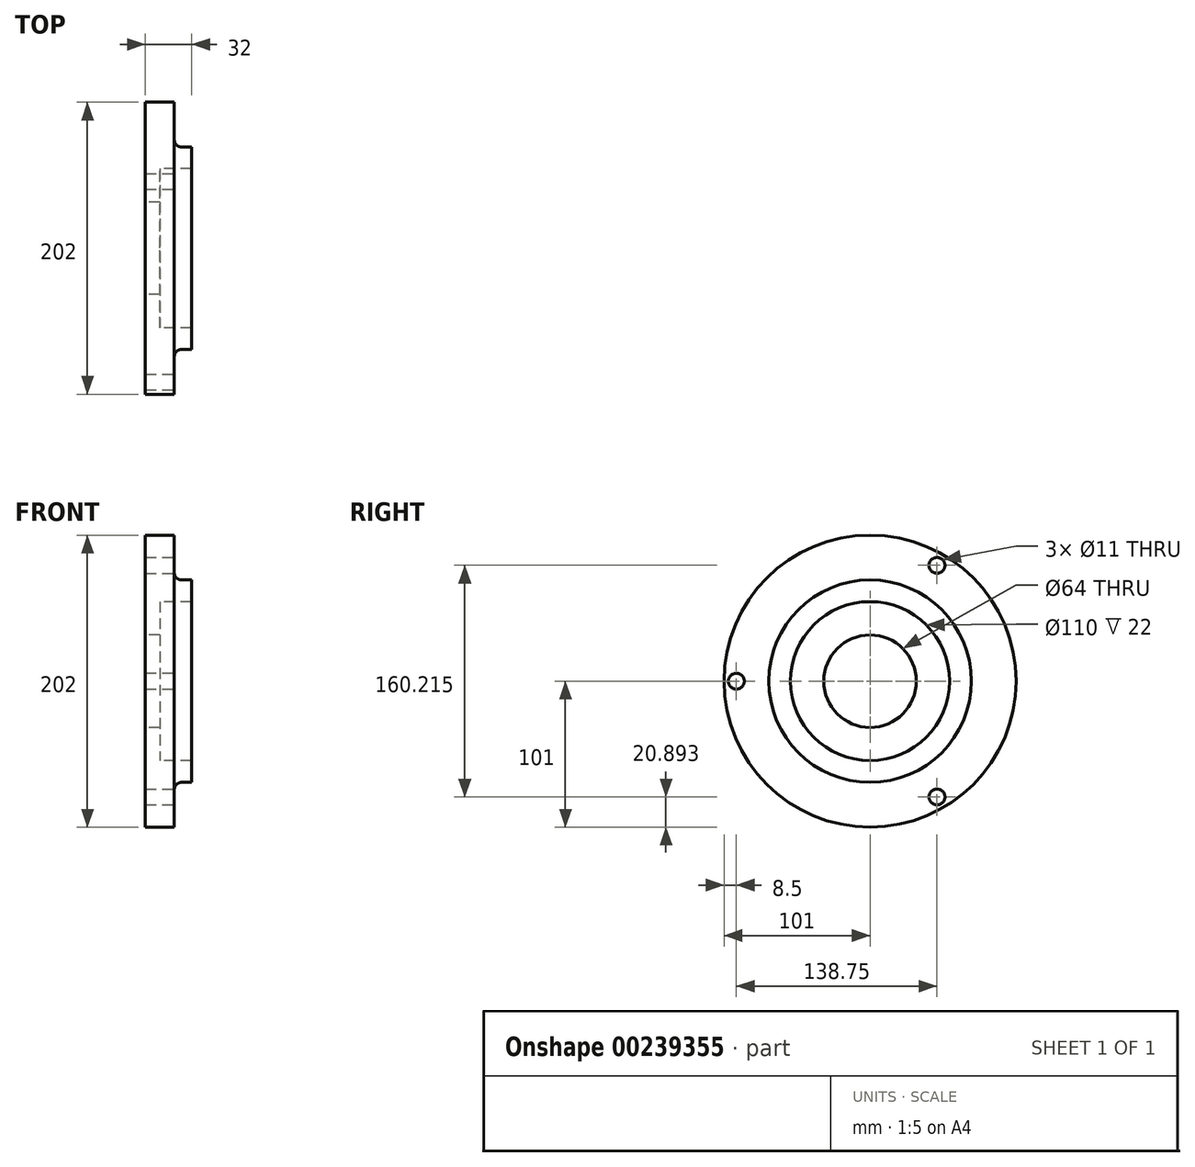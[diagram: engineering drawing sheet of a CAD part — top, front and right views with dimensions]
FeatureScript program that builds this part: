
annotation { "Feature Type Name" : "Feature", "Feature Type Description" : "" }
export const myFeature = defineFeature(function(context is Context, id is Id, definition is map)
    precondition{}
    {
        {
            var Q0;
            Q0=qCreatedBy(makeId("Front.planeOp"),FACE);
            var sketch = newSketch(context, id + "F0", { "sketchPlane" : qUnion([Q0])});
            skLineSegment(sketch, "E0", {"start": v(0, 32) * mm, "end": v(0, 101) * mm});
            skLineSegment(sketch, "E1", {"start": v(0, 101) * mm, "end": v(20, 101) * mm});
            skLineSegment(sketch, "E2", {"start": v(20, 101) * mm, "end": v(20, 70) * mm});
            skLineSegment(sketch, "E3", {"start": v(20, 70) * mm, "end": v(32, 70) * mm});
            skLineSegment(sketch, "E4", {"start": v(32, 70) * mm, "end": v(32, 55) * mm});
            skLineSegment(sketch, "E5", {"start": v(10, 32) * mm, "end": v(0, 32) * mm});
            skLineSegment(sketch, "E6", {"start": v(0, 0) * mm, "end": v(173.85, 0) * mm, "construction": true});
            skLineSegment(sketch, "E7", {"start": v(10, 55) * mm, "end": v(10, 32) * mm});
            skLineSegment(sketch, "E8", {"start": v(10, 55) * mm, "end": v(32, 55) * mm});
            skSolve(sketch);
        }
        {
            var Q0;
            Q0 = qSketchRegion(id + "F0", true);
            var Q1;
            Q1=sQuery(id+"F0.wireOp",EDGE,"E6");
            revolve(context, id + "F1", {"entities" : qUnion([Q0]), "axis" : qUnion([Q1]), "revolveType" : RevolveType.FULL});
        }
        {
            var Q0;
            Q0=makeQuery(id+"F1.opRevolve","SWEPT_EDGE",EDGE,{"disambiguationData":[OSD([sQuery(id+"F0.wireOp",EDGE,"E2"),sQuery(id+"F0.wireOp",EDGE,"E3")])]});
            fillet(context, id + "F2", {"entities" : qUnion([Q0]), "radius" : 5 * mm, "tangentPropagation" : true, "allowEdgeOverflow" : false});
        }
        {
            var Q0;
            Q0=makeQuery(id+"F1.opRevolve","SWEPT_FACE",FACE,{"disambiguationData":[OSD([sQuery(id+"F0.wireOp",EDGE,"E2")])]});
            var sketch = newSketch(context, id + "F3", { "sketchPlane" : qUnion([Q0])});
            skCircle(sketch, "E9", {"center": v(0, 0) * mm, "radius": 92.5 * mm, "construction": true});
            skPoint(sketch, "E10", {"position": v(-92.5, 0) * mm});
            skLineSegment(sketch, "E11", {"start": v(0, 0) * mm, "end": v(46.25, 80.1) * mm});
            skLineSegment(sketch, "E12", {"start": v(0, 0) * mm, "end": v(46.25, -80.1) * mm});
            skPoint(sketch, "E13", {"position": v(46.25, 80.1) * mm});
            skPoint(sketch, "E14", {"position": v(46.25, -80.1) * mm});
            skSolve(sketch);
        }
        {
            var Q0;
            Q0=sQuery(id+"F3.wireOp",VERTEX,"E13");
            var Q1;
            Q1=sQuery(id+"F3.wireOp",VERTEX,"E10");
            var Q2;
            Q2=sQuery(id+"F3.wireOp",VERTEX,"E14");
            var Q3;
            Q3=makeQuery(id+"F1.opRevolve","SWEPT_BODY",BODY,{"disambiguationData":[OSD([sQuery(id+"F0.wireOp",EDGE,"E0"),sQuery(id+"F0.wireOp",EDGE,"E1"),sQuery(id+"F0.wireOp",EDGE,"E2"),sQuery(id+"F0.wireOp",EDGE,"E3"),sQuery(id+"F0.wireOp",EDGE,"E4"),sQuery(id+"F0.wireOp",EDGE,"WVFCKdJw-IPtT-nuJO-PAan-GPxTuYcyGPCh"),sQuery(id+"F0.wireOp",EDGE,"zR6N78EG-2YPw-ovPM-uVPD-yJN4zuy4HvIG"),sQuery(id+"F0.wireOp",EDGE,"E5")])]});
            hole(context, id + "F4", {"style" : HoleStyle.SIMPLE, "endStyle" : HoleEndStyle.THROUGH, "standardTappedOrClearance" : lookupTablePath({ "standard" : "ISO", "fit" : "Normal", "size" : "M10", "type" : "Clearance" }), "standardBlindInLast" : lookupTablePath({ "fit" : "Standard", "standard" : "ISO", "size" : "M10", "type" : "Clearance" }), "holeDiameter" : 11 * mm, "locations" : qUnion([Q0, Q1, Q2]), "scope" : qUnion([Q3]), "isTappedThrough" : true});
        }
    });
